# Revit family: Viking Roofspec Sump 06 M18
name_source: partatom
category: Pipe Fittings
units: mm (PartAtom-declared; Revit-internal decimal feet)

## family parameters
Cut with Voids When Loaded = No
Host = Face
Part Type = Cap
Round Connector Dimension = Use Diameter
Shared = No

## types (1)
- Sumps - (with Weldable Flange) - IMR130T 580x380x249mmd+200mm outlet
    Component = IMR130T
    Default Elevation = 0 mm  [stored 0 ft]
    Flange Cut Length = 580 mm  [stored 1.90289 ft]
    Flange Cut Width = 380 mm  [stored 1.24672 ft]
    Flow Out = 10.0 L/s
    Manufacturer = Viking Roofspec
    Material = Viking Roofspec - Plastic White
    Model = IMR130T
    Offset Pipe1 = 137 mm  [stored 0.449475 ft]
    Offset Pipe2 = 114 mm  [stored 0.374016 ft]
    Overall Height = 389 mm  [stored 1.27625 ft]
    Pipe Diameter = 200 mm  [stored 0.656168 ft]
    Type Comments = Viking Roofspec sump / overflow IMR130T TPO weldable, installed as per manufacturers instructions.
    URL = www.vikingroofspec.co.nz

note: [stored X ft] marks values corroborated as IEEE doubles in the binary element streams (Revit-internal decimal feet)

## geometry (parser evidence)
native form markers: Sweep x26
no freeform markers — native parametric forms only
